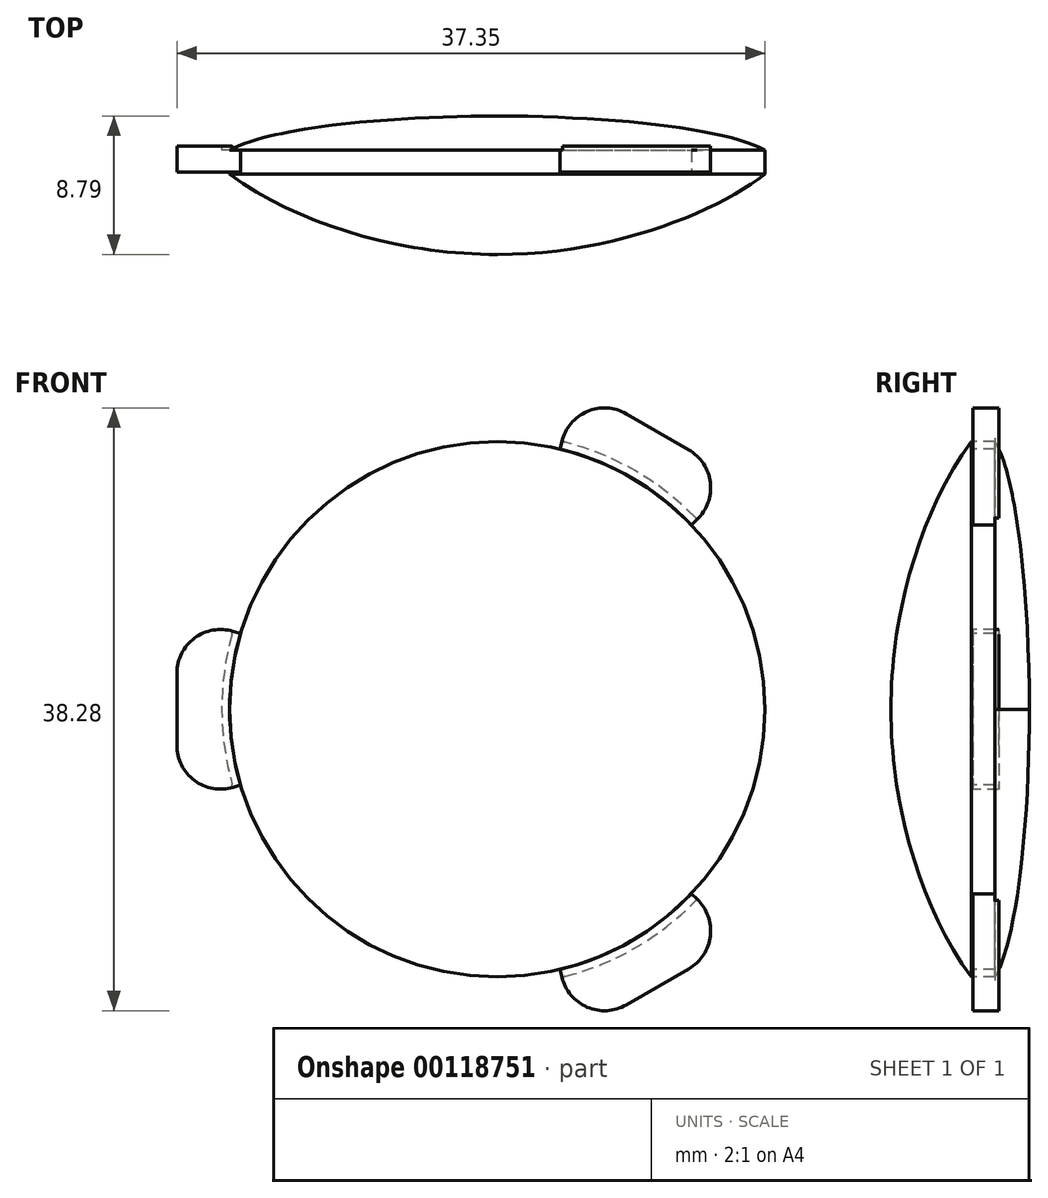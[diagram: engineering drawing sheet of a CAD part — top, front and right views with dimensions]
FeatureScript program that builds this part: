
annotation { "Feature Type Name" : "Feature", "Feature Type Description" : "" }
export const myFeature = defineFeature(function(context is Context, id is Id, definition is map)
    precondition{}
    {
        {
            var Q0;
            Q0=qCreatedBy(makeId("Top.planeOp"),FACE);
            var sketch = newSketch(context, id + "F0", { "sketchPlane" : qUnion([Q0])});
            skLineSegment(sketch, "E0", {"start": v(0, 0.75) * mm, "end": v(0, -0.75) * mm});
            skLineSegment(sketch, "E1", {"start": v(0, 0.75) * mm, "end": v(17, 0.75) * mm});
            skLineSegment(sketch, "E2", {"start": v(17, 0.75) * mm, "end": v(17, -0.75) * mm});
            skLineSegment(sketch, "E3", {"start": v(17, -0.75) * mm, "end": v(0, -0.75) * mm});
            skFitSpline(sketch, "E4", {"points": [v(17, 0.75) * mm, v(0, 2.92) * mm], "startDerivative": vector(-6.76, 4.03) * mm, "endDerivative": vector(-22.34, 0) * mm});
            skFitSpline(sketch, "E5", {"points": [v(17, -0.75) * mm, v(0, -5.87) * mm], "startDerivative": vector(-9.4, -7.3) * mm, "endDerivative": vector(-22.36, 0) * mm});
            skLineSegment(sketch, "E6", {"start": v(0, 0.75) * mm, "end": v(0, 2.92) * mm});
            skLineSegment(sketch, "E7", {"start": v(0, -0.75) * mm, "end": v(0, -5.87) * mm});
            skSolve(sketch);
        }
        {
            var Q0;
            Q0=makeQuery(id+"F0.imprint","IMPRINT",FACE,{"disambiguationData":[TD([[makeQuery(id+"F0.imprint","IMPRINT",EDGE,{"derivedFrom":sQuery(id+"F0.wireOp",EDGE,"E1")}),1.0]])]});
            var Q1;
            Q1=makeQuery(id+"F0.imprint","IMPRINT",FACE,{"disambiguationData":[TD([[makeQuery(id+"F0.imprint","IMPRINT",EDGE,{"derivedFrom":sQuery(id+"F0.wireOp",EDGE,"E0")}),1.0]])]});
            var Q2;
            Q2=makeQuery(id+"F0.imprint","IMPRINT",FACE,{"disambiguationData":[TD([[makeQuery(id+"F0.imprint","IMPRINT",EDGE,{"derivedFrom":sQuery(id+"F0.wireOp",EDGE,"E3")}),1.0]])]});
            var Q3;
            Q3=sQuery(id+"F0.wireOp",EDGE,"E6");
            revolve(context, id + "F1", {"entities" : qUnion([Q0, Q1, Q2]), "axis" : qUnion([Q3]), "revolveType" : RevolveType.FULL});
        }
        {
            var Q0;
            Q0=qCreatedBy(makeId("Front.planeOp"),FACE);
            var sketch = newSketch(context, id + "F2", { "sketchPlane" : qUnion([Q0])});
            skCircle(sketch, "E8.0", {"center": v(0, 0) * mm, "radius": 17 * mm});
            skLineSegment(sketch, "E9", {"start": v(-20.35, 2.3) * mm, "end": v(-20.35, 0) * mm});
            skPoint(sketch, "E10.visualSharp", {"position": v(-20.35, 6.08) * mm});
            skArc(sketch, "E10.filletArc", {"start": v(-16.78, 4.96) * mm, "mid": v(-19.23, 4.52) * mm, "end": v(-20.35, 2.3) * mm});
            skLineSegment(sketch, "E11", {"start": v(-16.78, 4.96) * mm, "end": v(-16.3, 4.82) * mm});
            skLineSegment(sketch, "E12.MirrorCS", {"start": v(-20.35, -2.3) * mm, "end": v(-20.35, 0) * mm});
            skLineSegment(sketch, "E13.MirrorCS", {"start": v(-16.78, -4.96) * mm, "end": v(-16.3, -4.82) * mm});
            skPoint(sketch, "E14.MirrorP", {"position": v(-20.35, -6.08) * mm});
            skArc(sketch, "E15.MirrorCS", {"start": v(-16.78, -4.96) * mm, "mid": v(-19.23, -4.52) * mm, "end": v(-20.35, -2.3) * mm});
            skArc(sketch, "E16.0", {"start": v(-16.78, 4.96) * mm, "mid": v(-17.5, 0) * mm, "end": v(-16.78, -4.96) * mm});
            skSolve(sketch);
        }
        {
            var Q0;
            {var subQ5=sQuery(id+"F2.wireOp",EDGE,"ea668e26-e1b3-46df-957d-3e8b0d69fa4e.0");Q0=makeQuery(id+"F2.imprint","IMPRINT",FACE,{"disambiguationData":[TD([[makeQuery(id+"F2.imprint","IMPRINT",EDGE,{"derivedFrom":subQ5}),1.0]])]});}
            var Q1;
            {var subQ4=sQuery(id+"F2.wireOp",EDGE,"E9");Q1=makeQuery(id+"F2.imprint","IMPRINT",FACE,{"disambiguationData":[TD([[makeQuery(id+"F2.imprint","IMPRINT",EDGE,{"derivedFrom":subQ4}),1.0]])]});}
            var Q2;
            {var subQ0=sQuery(id+"F2.wireOp",EDGE,"E11");Q2=makeQuery(id+"F2.imprint","IMPRINT",FACE,{"disambiguationData":[TD([[makeQuery(id+"F2.imprint","IMPRINT",EDGE,{"derivedFrom":subQ0}),-1.0]])]});}
            extrude(context, id + "F3", {"entities" : qUnion([Q0, Q1, Q2]), "oppositeDirection" : true, "depth" : (1.5 / 2) * mm, "hasSecondDirection" : true, "secondDirectionOppositeDirection" : false, "secondDirectionDepth" : (1.5 / 2 - .1) * mm});
        }
        {
            var Q0;
            {var subQ4=sQuery(id+"F2.wireOp",EDGE,"E9");Q0=makeQuery(id+"F2.imprint","IMPRINT",FACE,{"disambiguationData":[TD([[makeQuery(id+"F2.imprint","IMPRINT",EDGE,{"derivedFrom":subQ4}),1.0]])]});}
            extrude(context, id + "F4", {"entities" : qUnion([Q0]), "operationType" : NewBodyOperationType.ADD, "oppositeDirection" : true, "depth" : (1.5 / 2 + .25) * mm});
        }
        {
            var Q0;
            Q0=makeQuery(id+"F4.opExtrude","SWEPT_EDGE",EDGE,{"disambiguationData":[OSD([sQuery(id+"F2.wireOp",EDGE,"E13.MirrorCS"),sQuery(id+"F2.wireOp",EDGE,"E15.MirrorCS"),sQuery(id+"F2.wireOp",EDGE,"E16.0")])]});
            var Q1;
            Q1=makeQuery(id+"F4.opExtrude","SWEPT_EDGE",EDGE,{"disambiguationData":[OSD([sQuery(id+"F2.wireOp",EDGE,"E10.filletArc"),sQuery(id+"F2.wireOp",EDGE,"E11"),sQuery(id+"F2.wireOp",EDGE,"E16.0")])]});
            fillet(context, id + "F5", {"entities" : qUnion([Q0, Q1]), "radius" : 0.2 * mm, "tangentPropagation" : true, "allowEdgeOverflow" : false});
        }
        {
            var Q0;
            Q0=makeQuery(id+"F3.opExtrude","SWEPT_BODY",BODY,{"disambiguationData":[OSD([sQuery(id+"F2.wireOp",EDGE,"E8.0"),sQuery(id+"F2.wireOp",EDGE,"E9"),sQuery(id+"F2.wireOp",EDGE,"E10.filletArc"),sQuery(id+"F2.wireOp",EDGE,"c27d5dee-d282-4062-965e-ce4ce2b370330.MirrorCS"),sQuery(id+"F2.wireOp",EDGE,"d57db254-61b6-49c5-9390-629f8352e29f0.MirrorCS")])]});
            var Q1;
            Q1=sQuery(id+"F0.wireOp",EDGE,"E7");
            circularPattern(context, id + "F6", {"operationType" : NewBodyOperationType.ADD, "entities" : qUnion([Q0]), "axis" : qUnion([Q1]), "angle" : 120 * degree, "instanceCount" : 3});
        }
    });
